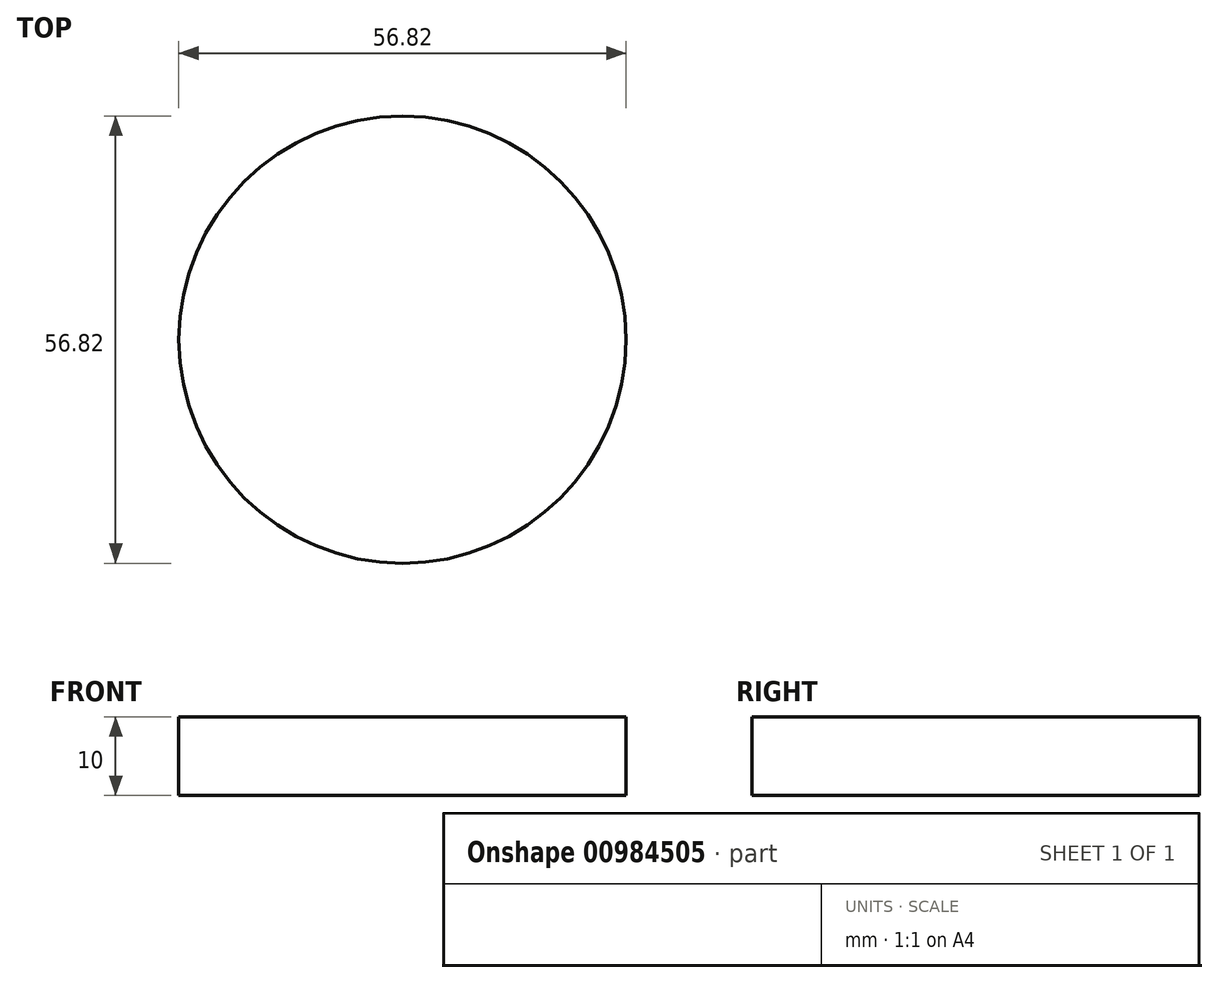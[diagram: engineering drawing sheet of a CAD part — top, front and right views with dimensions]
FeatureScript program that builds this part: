
annotation { "Feature Type Name" : "Feature", "Feature Type Description" : "" }
export const myFeature = defineFeature(function(context is Context, id is Id, definition is map)
    precondition{}
    {
        {
            var Q0;
            Q0=qCreatedBy(makeId("Top.planeOp"),FACE);
            var sketch = newSketch(context, id + "F0", { "sketchPlane" : qUnion([Q0])});
            skCircle(sketch, "E0", {"center": v(0, 0) * mm, "radius": 28.4 * mm});
            skSolve(sketch);
        }
        {
            var Q0;
            Q0 = qSketchRegion(id + "F0", false);
            extrude(context, id + "F1", {"entities" : qUnion([Q0]), "depth" : 10 * mm});
        }
    });
